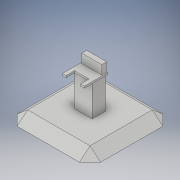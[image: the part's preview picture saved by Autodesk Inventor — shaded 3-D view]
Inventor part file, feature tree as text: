
AUTODESK INVENTOR PART (.ipt)
format: ipt  version: 2017 (Build 210142000, 142)  size: 407,552 bytes
history: native  units: in
note: dims shown in document units (in); Inventor stores cm internally (conversion verified against a paired STEP export)
features: other x10, extrude x8, sketch x7, pattern_circular x2, loft x2, plane x1
ambient origin geometry x7: Origin, YZ Plane, XY Plane, X Axis, Y Axis, Z Axis, Center Point
bodies: Solid4 (feature_tree)
feature tree (30):
  other  "bace + terminal"
  extrude  "base stand"  Depth=1.0in
  extrude  "arm rests and terminal monitor"  Depth=0.85in
  other  "middle of the part vertical"
  other  "used to line up the key board and mouse"
  extrude  "bace"  Depth=0.75in
  extrude  "ramp to terminal"  Depth=1.0in
  pattern_circular  "made rest of ramps to terminal"  [2 undecoded]
  loft  "smooth edges of base"
  pattern_circular  "rest of the smooth edges of base"  [2 undecoded]
  other  "mate to back to monitor"
  extrude  "monitor raise"  Depth=0.2083in TaperAngle=0.0deg
  sketch  "Sketch26"  dims[d27=1.1in d28=0.75in]
  plane  "Work Plane20"
  loft  "outlet cap"
  sketch  "Sketch28"  dims[d29=1.0in d30=0.65in]
  extrude  "outlet revele out"  Depth=0.0181in
  extrude  "hot and ground wire holes"  Depth=1.125in
  other  "screw workplane"
  other  "screw made"
  extrude  "slot for screw"  Depth=1.0in TaperAngle=0.0deg
  other  "bottom workplane"
  other  "bace of terminal"
  sketch  "Sketch23"  dims[d0=1.0in d1=0.75in]
  sketch  "Sketch25"  dims[d19=1.2in d20=0.85in]
  sketch  "Sketch29"  dims[d42=1.1in d43=0.85in d44=1.0in d45=0.75in d49=1.2in d50=0.85in d51=1.0in d52=0.75in]
  sketch  "Sketch30"  dims[d123=1.0in d124=0.0in]
  sketch  "Sketch31"  dims[d163=0.8125in d165=0.4167in d166=0.8125in d167=0.4167in d168=0.2083in d169=0.0in d170=1.125in d173=1.8892in d175=1.125in d178=1.0in d179=0.0in d182=0.2318in d183=0.3777in d185=0.05in d186=0.0678in d188=0.1962in d189=0.3421in d190=0.0in d191=90.0deg d192=0.0in d193=90.0deg d194=0.0251in d195=0.0305in d197=0.0931in d198=0.0311in d199=0.0362in d200=0.0045in d201=0.0208in d202=0.0208in d203=0.0078in d204=0.0291in d205=0.0078in d206=0.0362in d207=0.0045in d208=0.0208in d209=0.0078in d211=0.0078in d212=0.0208in d213=0.0181in d214=0.0291in d221=0.003in d222=0.0in d223=0.0649in d224=0.0in d225=90.0deg d226=0.0108in d227=0.0027in d228=90.0deg d229=0.0015in d230=0.0128in d231=0.0in d232=3.6493in d233=0.0in d234=0.1564in d235=0.2069in d236=7.0in d237=7.0in d238=0.2749in d239=3.6493in d240=0.0in d241=1.5748in d242=360.0deg d244=0.0in d245=0.5527in d246=2.2315in d247=0.1134in d248=0.0181in d253=0.0in d254=90.0deg d255=0.0in d256=90.0deg d257=1.5748in d258=360.0deg]
  other  "Edges4"
  other  "Edges5"
note: 4 required parameter values undecoded (feature->parameter linkage not recoverable at this tier; creation-order binding heuristic only, values carry confidence <= 0.55)
